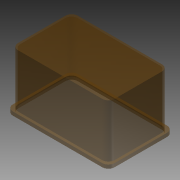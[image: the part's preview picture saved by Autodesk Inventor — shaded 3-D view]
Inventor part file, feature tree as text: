
AUTODESK INVENTOR PART (.ipt)
format: ipt  version: 2015 SP1 (Build 190203100, 203)  size: 146,432 bytes
history: native  units: mm
features: extrude x3, sketch x3, fillet x1
ambient origin geometry x8: Origin, YZ Plane, XZ Plane, XY Plane, X Axis, Y Axis, Z Axis, Center Point
bodies: Solid1 (feature_tree)
feature tree (7):
  extrude  "Extrusion1"  Depth=187.5mm
  fillet  "Fillet1"  Radius=5.0mm
  extrude  "Extrusion2"  Depth=5.0mm
  extrude  "Extrusion3"  Depth=7.0mm TaperAngle=0.0deg
  sketch  "Sketch1"  dims[d0=116.0mm d1=187.5mm d2=5.0mm]
  sketch  "Sketch2"  dims[d3=5.0mm d4=5.0mm]
  sketch  "Sketch3"  dims[d5=5.0mm d6=7.0mm d7=0.0mm d8=12.0mm d9=2.0mm d10=2.0mm d11=2.0mm d12=2.0mm d13=12.0mm d14=103.0mm d15=0.0mm d16=2.0mm d17=0.0mm]
